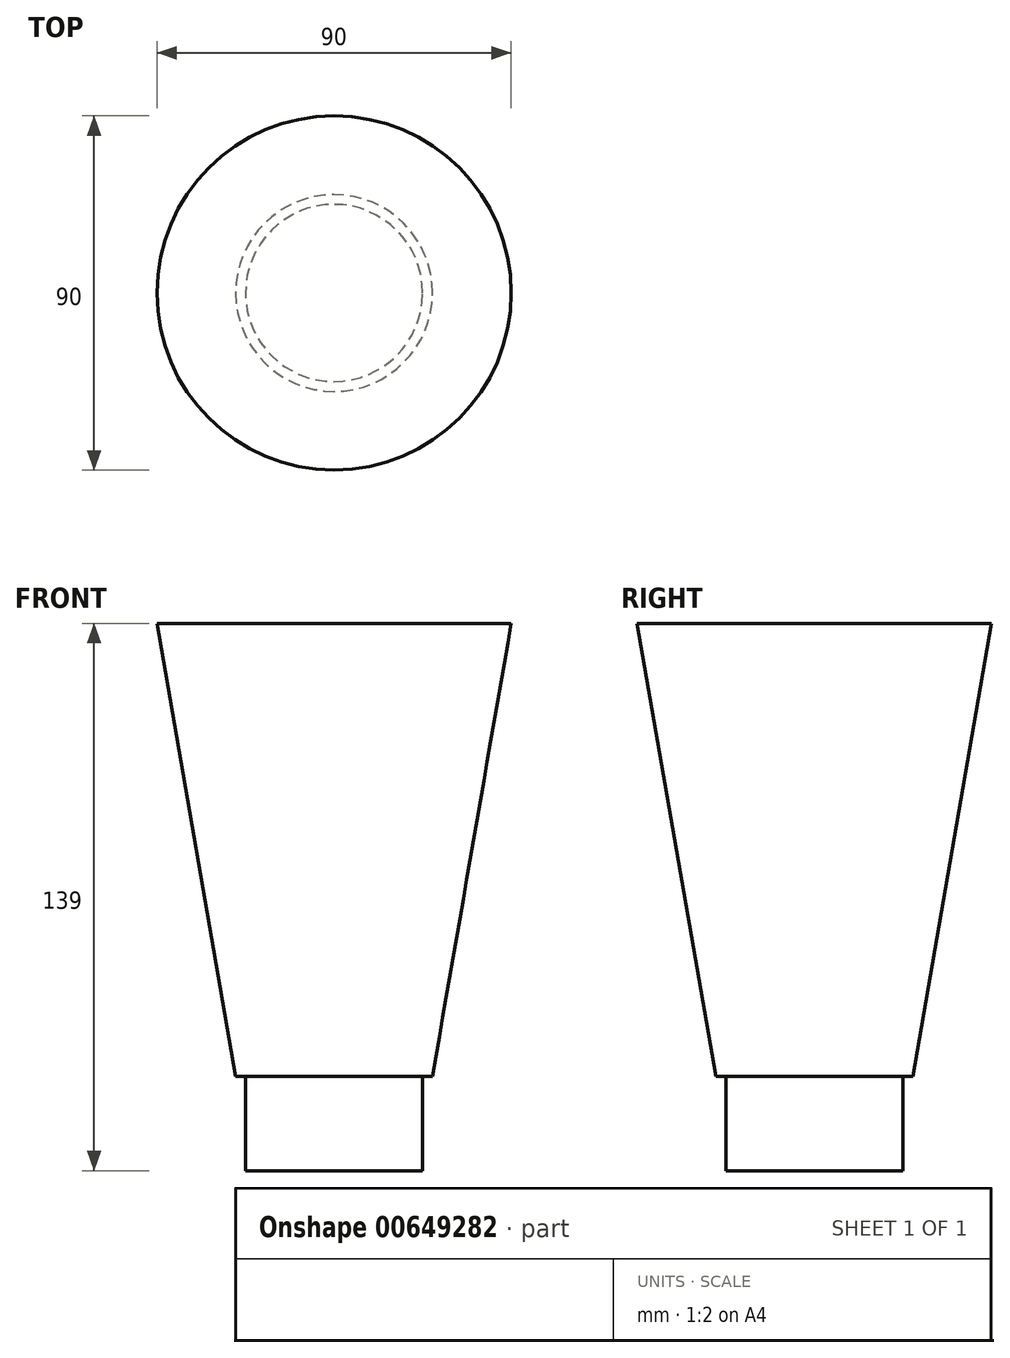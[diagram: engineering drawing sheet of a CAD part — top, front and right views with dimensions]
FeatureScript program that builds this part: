
annotation { "Feature Type Name" : "Feature", "Feature Type Description" : "" }
export const myFeature = defineFeature(function(context is Context, id is Id, definition is map)
    precondition{}
    {
        {
            var Q0;
            Q0=qCreatedBy(makeId("Top.planeOp"),FACE);
            var sketch = newSketch(context, id + "F0", { "sketchPlane" : qUnion([Q0])});
            skCircle(sketch, "E0", {"center": v(0, 0) * mm, "radius": 45 * mm});
            skSolve(sketch);
        }
        {
            var Q0;
            Q0 = qSketchRegion(id + "F0", true);
            extrude(context, id + "F1", {"entities" : qUnion([Q0]), "depth" : 115 * mm, "offsetDistance" : 25 * mm});
        }
        {
            var Q0;
            Q0=makeQuery(id+"F1.opExtrude","CAP_FACE",FACE,{"disambiguationData":[OSD([sQuery(id+"F0.wireOp",EDGE,"E0")])],"isStart":true});
            var sketch = newSketch(context, id + "F2", { "sketchPlane" : qUnion([Q0])});
            skCircle(sketch, "E1", {"center": v(0, 0) * mm, "radius": 22.5 * mm});
            skSolve(sketch);
        }
        {
            var Q0;
            Q0 = qSketchRegion(id + "F2", true);
            extrude(context, id + "F3", {"entities" : qUnion([Q0]), "operationType" : NewBodyOperationType.ADD, "depth" : 24 * mm, "offsetDistance" : 25 * mm});
        }
        {
            var Q0;
            Q0=makeQuery(id+"F1.opExtrude","CAP_EDGE",EDGE,{"disambiguationData":[OSD([sQuery(id+"F0.wireOp",EDGE,"E0")])],"isStart":true});
            chamfer(context, id + "F4", {"entities" : qUnion([Q0]), "chamferType" : ChamferType.TWO_OFFSETS, "width1" : 20 * mm, "oppositeDirection" : true, "width2" : 115 * mm, "tangentPropagation" : true});
        }
    });
